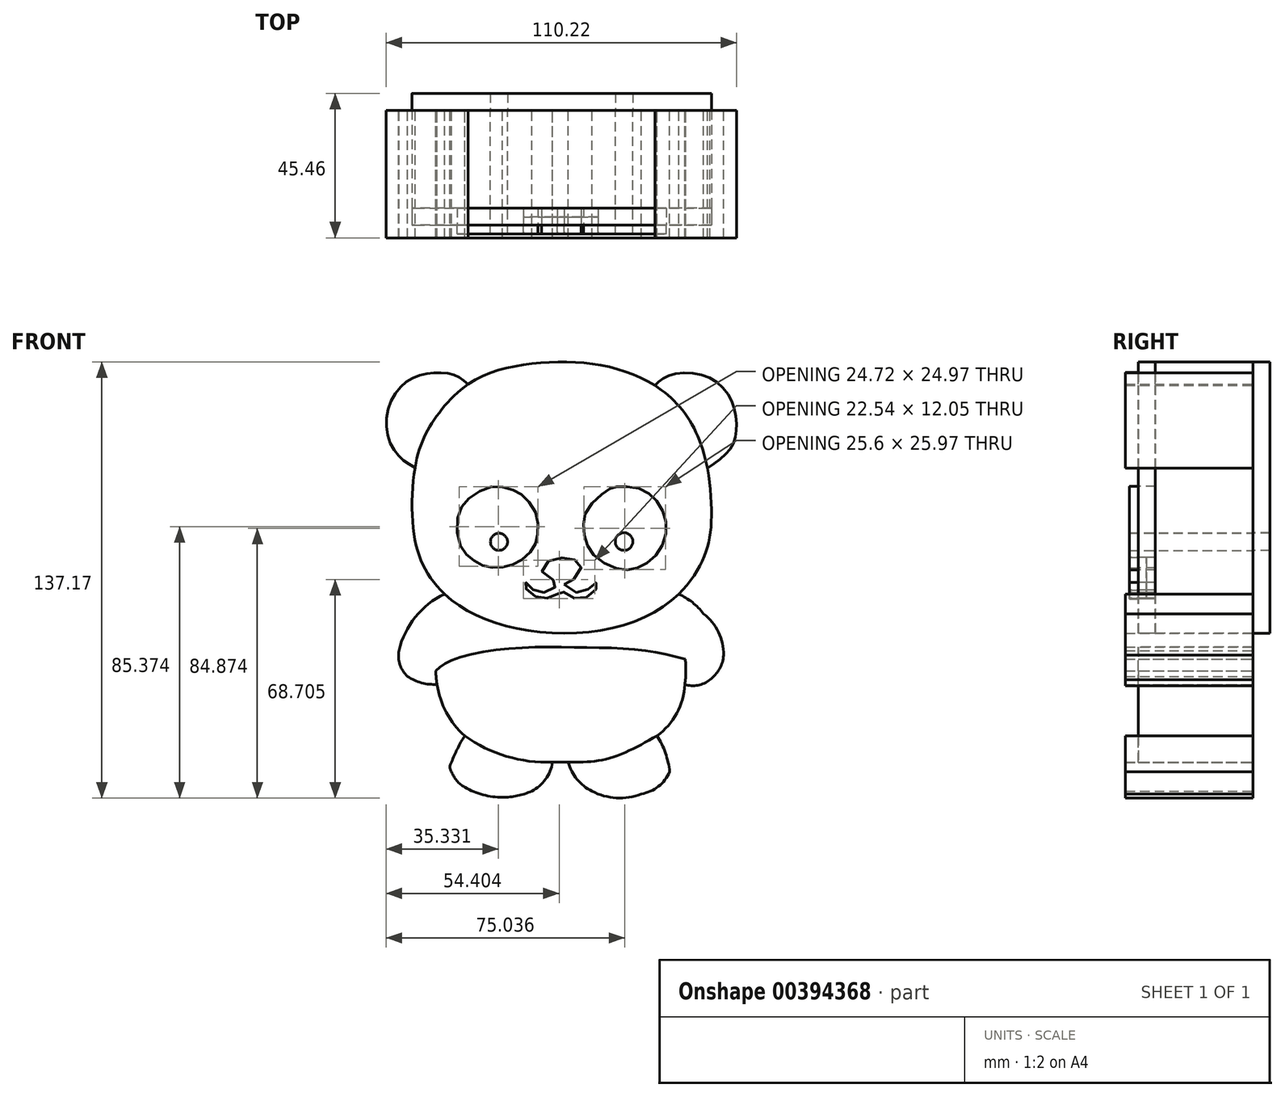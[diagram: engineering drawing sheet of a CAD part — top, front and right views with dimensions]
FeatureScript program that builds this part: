
annotation { "Feature Type Name" : "Feature", "Feature Type Description" : "" }
export const myFeature = defineFeature(function(context is Context, id is Id, definition is map)
    precondition{}
    {
        {
            var Q0;
            Q0=qCreatedBy(makeId("Front.planeOp"),FACE);
            var sketch = newSketch(context, id + "F0", { "sketchPlane" : qUnion([Q0])});
            skFitSpline(sketch, "E0", {"points": [v(-35.08, 45.27) * mm, v(-23.68, 56.67) * mm, v(-7.72, 61.99) * mm, v(10.34, 62.75) * mm, v(26.87, 59.14) * mm, v(40.17, 50.59) * mm, v(49.1, 35.2) * mm, v(51.76, 13.72) * mm, v(49.48, 1.75) * mm, v(40.74, -10.8) * mm, v(21.17, -20.67) * mm, v(-6.39, -21.43) * mm, v(-26.53, -14.4) * mm, v(-37.36, -3.76) * mm, v(-41.92, 9.92) * mm, v(-40.97, 32.15) * mm, v(-35.08, 45.27) * mm]});
            skFitSpline(sketch, "E1", {"points": [v(-41.46, 29.63) * mm, v(-47.62, 34.62) * mm, v(-50.47, 45.27) * mm, v(-45.15, 55.9) * mm, v(-36.98, 59.33) * mm, v(-29.38, 58.95) * mm, v(-24.74, 55.97) * mm], "startDerivative": vector(-42.28, 25.45) * mm, "endDerivative": vector(31.77, -26.58) * mm});
            skFitSpline(sketch, "E2", {"points": [v(34, 55.54) * mm, v(38.25, 58.65) * mm, v(49.6, 58.65) * mm, v(57.74, 51.45) * mm, v(59.66, 42.19) * mm, v(57.58, 35.48) * mm, v(50.48, 29.52) * mm], "startDerivative": vector(26.51, 27.39) * mm, "endDerivative": vector(-48.08, -32.52) * mm});
            skFitSpline(sketch, "E3", {"points": [v(21.95, 23.65) * mm, v(29.3, 23.01) * mm, v(34.9, 18.7) * mm, v(37.6, 11.35) * mm, v(35.21, 3.36) * mm, v(29.14, -1.6) * mm, v(22.9, -2.24) * mm, v(14.44, 2.56) * mm, v(11.72, 9.1) * mm, v(12.52, 16.14) * mm, v(18.91, 22.53) * mm, v(21.95, 23.65) * mm]});
            skFitSpline(sketch, "E4", {"points": [v(-17.36, 23.65) * mm, v(-11.4, 22.95) * mm, v(-7.17, 20.53) * mm, v(-3.28, 14.96) * mm, v(-2.94, 8.57) * mm, v(-4.38, 4.24) * mm, v(-9.01, 0) * mm, v(-13.77, -1.6) * mm, v(-19.12, -1.44) * mm, v(-23.36, 0.77) * mm, v(-27.05, 4.77) * mm, v(-28, 14.18) * mm, v(-24.66, 19.92) * mm, v(-17.36, 23.65) * mm]});
            skCircle(sketch, "E5", {"center": v(-15.05, 6.36) * mm, "radius": 2.68 * mm});
            skCircle(sketch, "E6", {"center": v(24.29, 6.46) * mm, "radius": 2.77 * mm});
            skFitSpline(sketch, "E7", {"points": [v(5.4, -7.03) * mm, v(9.84, -9.72) * mm, v(12.93, -8.5) * mm, v(15.08, -6.5) * mm, v(16.02, -6.9) * mm, v(15.48, -8.5) * mm, v(12.66, -11.06) * mm, v(9.16, -11.46) * mm, v(5.67, -9.85) * mm, v(4.6, -8.78) * mm, v(3.25, -10.26) * mm, v(0, -11.33) * mm, v(-3.33, -10.93) * mm, v(-6.02, -9.05) * mm, v(-7.36, -6.63) * mm, v(-6.02, -6.63) * mm, v(-4.4, -8.64) * mm, v(-1.45, -9.58) * mm, v(1.77, -8.5) * mm, v(3.25, -6.63) * mm, v(0, -4.61) * mm, v(-1.58, -1.52) * mm, v(2.98, 1.3) * mm, v(6.34, 1.17) * mm, v(10.24, 0) * mm, v(10.64, -2.46) * mm, v(7.42, -6.09) * mm, v(5.4, -7.03) * mm]});
            skArc(sketch, "E8", {"start": v(-32.16, -10.06) * mm, "mid": v(-41.36, -17.31) * mm, "end": v(-46.5, -27.85) * mm});
            skArc(sketch, "E9", {"start": v(-46.5, -27.85) * mm, "mid": v(-46.2, -32.27) * mm, "end": v(-43.8, -35.99) * mm});
            skArc(sketch, "E10", {"start": v(-43.8, -35.99) * mm, "mid": v(-39.37, -37.98) * mm, "end": v(-34.54, -38.47) * mm});
            skArc(sketch, "E11", {"start": v(-30.35, -17.77) * mm, "mid": v(-34.36, -27.73) * mm, "end": v(-34.54, -38.47) * mm});
            skArc(sketch, "E12", {"start": v(-34.54, -38.47) * mm, "mid": v(-31.6, -47.33) * mm, "end": v(-25.83, -54.65) * mm});
            skArc(sketch, "E13", {"start": v(-25.83, -54.65) * mm, "mid": v(-12.7, -61.09) * mm, "end": v(1.81, -62.96) * mm});
            skArc(sketch, "E14", {"start": v(-4.76, -72.06) * mm, "mid": v(-0.4, -68.28) * mm, "end": v(1.81, -62.96) * mm});
            skArc(sketch, "E15", {"start": v(-13.91, -73.98) * mm, "mid": v(-9.24, -73.5) * mm, "end": v(-4.76, -72.06) * mm});
            skArc(sketch, "E16", {"start": v(-25.83, -70.81) * mm, "mid": v(-20.08, -73.2) * mm, "end": v(-13.91, -73.98) * mm});
            skArc(sketch, "E17", {"start": v(-29.96, -65.96) * mm, "mid": v(-28.32, -68.74) * mm, "end": v(-25.83, -70.81) * mm});
            skArc(sketch, "E18", {"start": v(-29.96, -62.96) * mm, "mid": v(-30.47, -64.46) * mm, "end": v(-29.96, -65.96) * mm});
            skArc(sketch, "E19", {"start": v(-25.83, -54.65) * mm, "mid": v(-28.14, -58.68) * mm, "end": v(-29.96, -62.96) * mm});
            skArc(sketch, "E20", {"start": v(38.63, -65.96) * mm, "mid": v(37.31, -60.07) * mm, "end": v(34.67, -54.65) * mm});
            skArc(sketch, "E21", {"start": v(29.7, -72.96) * mm, "mid": v(35.05, -70.6) * mm, "end": v(38.63, -65.96) * mm});
            skArc(sketch, "E22", {"start": v(6.76, -62.96) * mm, "mid": v(9.5, -68.32) * mm, "end": v(14.22, -72.06) * mm});
            skArc(sketch, "E23", {"start": v(14.22, -72.06) * mm, "mid": v(21.86, -74.18) * mm, "end": v(29.7, -72.96) * mm});
            skArc(sketch, "E24", {"start": v(34.67, -54.65) * mm, "mid": v(40.87, -47.56) * mm, "end": v(43.38, -38.47) * mm});
            skArc(sketch, "E25", {"start": v(43.38, -38.47) * mm, "mid": v(43.02, -27.8) * mm, "end": v(38.63, -18.07) * mm});
            skArc(sketch, "E26", {"start": v(43.38, -38.47) * mm, "mid": v(47.55, -38.77) * mm, "end": v(51.31, -36.95) * mm});
            skArc(sketch, "E27", {"start": v(51.31, -36.95) * mm, "mid": v(54.32, -33.6) * mm, "end": v(55.61, -29.3) * mm});
            skArc(sketch, "E28", {"start": v(55.61, -29.3) * mm, "mid": v(53.98, -22.04) * mm, "end": v(49.3, -16.26) * mm});
            skArc(sketch, "E29", {"start": v(49.3, -16.26) * mm, "mid": v(45.78, -12.68) * mm, "end": v(41.49, -10.1) * mm});
            skArc(sketch, "E30", {"start": v(45.78, -9.36) * mm, "mid": v(53.67, 8.21) * mm, "end": v(53.98, 27.47) * mm});
            skPoint(sketch, "E30.startSnap0", {"position": v(45.78, -12.68) * mm});
            skPoint(sketch, "E30.endSnap0", {"position": v(53.98, -22.04) * mm});
            skArc(sketch, "E31", {"start": v(58.54, -27.85) * mm, "mid": v(54.79, -16.79) * mm, "end": v(45.78, -9.36) * mm});
            skArc(sketch, "E32", {"start": v(51.31, -41.07) * mm, "mid": v(56.55, -35.35) * mm, "end": v(58.54, -27.85) * mm});
            skArc(sketch, "E33", {"start": v(45.78, -41.07) * mm, "mid": v(48.55, -41.66) * mm, "end": v(51.31, -41.07) * mm});
            skArc(sketch, "E34", {"start": v(38.63, -54.65) * mm, "mid": v(43.06, -48.31) * mm, "end": v(45.78, -41.07) * mm});
            skArc(sketch, "E35", {"start": v(40.74, -68.63) * mm, "mid": v(40.88, -61.46) * mm, "end": v(38.63, -54.65) * mm});
            skArc(sketch, "E36", {"start": v(29.38, -76) * mm, "mid": v(35.79, -73.44) * mm, "end": v(40.74, -68.63) * mm});
            skArc(sketch, "E37", {"start": v(4.3, -65.96) * mm, "mid": v(8.42, -71.56) * mm, "end": v(14.22, -75.4) * mm});
            skArc(sketch, "E38", {"start": v(14.22, -75.4) * mm, "mid": v(21.75, -76.81) * mm, "end": v(29.38, -76) * mm});
            skArc(sketch, "E39", {"start": v(-4.76, -75.4) * mm, "mid": v(0.6, -71.48) * mm, "end": v(4.3, -65.96) * mm});
            skArc(sketch, "E40", {"start": v(-21.84, -76) * mm, "mid": v(-13.26, -76.9) * mm, "end": v(-4.76, -75.4) * mm});
            skArc(sketch, "E41", {"start": v(-32.12, -67.4) * mm, "mid": v(-27.89, -72.79) * mm, "end": v(-21.84, -76) * mm});
            skArc(sketch, "E42", {"start": v(-32.12, -62.96) * mm, "mid": v(-32.46, -65.18) * mm, "end": v(-32.12, -67.4) * mm});
            skArc(sketch, "E43", {"start": v(-29.96, -55.54) * mm, "mid": v(-31.2, -59) * mm, "end": v(-32.12, -62.54) * mm});
            skArc(sketch, "E44", {"start": v(-36.87, -41.87) * mm, "mid": v(-34.16, -49.08) * mm, "end": v(-29.96, -55.54) * mm});
            skArc(sketch, "E45", {"start": v(-49.5, -29.3) * mm, "mid": v(-45.59, -38) * mm, "end": v(-36.87, -41.87) * mm});
            skArc(sketch, "E46", {"start": v(-36.87, -9.36) * mm, "mid": v(-45.7, -17.73) * mm, "end": v(-49.5, -29.3) * mm});
            skArc(sketch, "E47", {"start": v(-43.8, 27.87) * mm, "mid": v(-44.76, 8.43) * mm, "end": v(-36.87, -9.36) * mm});
            skArc(sketch, "E48", {"start": v(-52.67, 39.14) * mm, "mid": v(-49.63, 32.4) * mm, "end": v(-43.8, 27.87) * mm});
            skArc(sketch, "E49", {"start": v(-50.3, 54.06) * mm, "mid": v(-52.52, 46.77) * mm, "end": v(-52.67, 39.14) * mm});
            skArc(sketch, "E50", {"start": v(-24.15, 59.33) * mm, "mid": v(-38.22, 61.64) * mm, "end": v(-50.3, 54.06) * mm});
            skArc(sketch, "E51", {"start": v(32.69, 59.14) * mm, "mid": v(4.3, 65.86) * mm, "end": v(-24.15, 59.33) * mm});
            skArc(sketch, "E52", {"start": v(53.98, 27.47) * mm, "mid": v(59.26, 54.01) * mm, "end": v(32.69, 59.14) * mm});
            skFitSpline(sketch, "E53", {"points": [v(-34.93, -34.2) * mm, v(-30.62, -31.16) * mm, v(-13.37, -27.32) * mm, v(9.96, -26.84) * mm, v(29.46, -27.64) * mm, v(43.51, -30.5) * mm], "startDerivative": vector(28.9, 26.69) * mm, "endDerivative": vector(69.5, -17.43) * mm});
            skFitSpline(sketch, "E54", {"points": [v(6.76, -62.96) * mm, v(19.43, -61.78) * mm, v(34.67, -54.65) * mm], "startDerivative": vector(26.94, 0.04) * mm, "endDerivative": vector(28.83, 16.2) * mm});
            skFitSpline(sketch, "E55", {"points": [v(1.81, -62.96) * mm, v(6.76, -62.96) * mm], "startDerivative": vector(4.95, 0) * mm, "endDerivative": vector(4.95, 0) * mm});
            skSolve(sketch);
        }
        {
            var Q0;
            Q0=makeQuery(id+"F0.imprint","IMPRINT",FACE,{"disambiguationData":[TD([[makeQuery(id+"F0.imprint","IMPRINT",EDGE,{"derivedFrom":sQuery(id+"F0.wireOp",EDGE,"E3")}),1.0]])]});
            var Q1;
            {var subQ1=sQuery(id+"F0.wireOp",EDGE,"E12");Q1=makeQuery(id+"F0.imprint","IMPRINT",FACE,{"disambiguationData":[TD([[makeQuery(id+"F0.imprint","IMPRINT",EDGE,{"derivedFrom":subQ1}),1.0]])]});}
            extrude(context, id + "F1", {"entities" : qUnion([Q0, Q1]), "depth" : 36.07 * mm});
        }
        {
            var Q0;
            {var subQ0=sQuery(id+"F0.wireOp",EDGE,"E1");Q0=makeQuery(id+"F0.imprint","IMPRINT",FACE,{"disambiguationData":[TD([[makeQuery(id+"F0.imprint","IMPRINT",EDGE,{"derivedFrom":subQ0}),-1.0]])]});}
            var Q1;
            {var subQ0=sQuery(id+"F0.wireOp",EDGE,"E2");Q1=makeQuery(id+"F0.imprint","IMPRINT",FACE,{"disambiguationData":[TD([[makeQuery(id+"F0.imprint","IMPRINT",EDGE,{"derivedFrom":subQ0}),-1.0]])]});}
            var Q2;
            {var subQ6=sQuery(id+"F0.wireOp",EDGE,"E8");Q2=makeQuery(id+"F0.imprint","IMPRINT",FACE,{"disambiguationData":[TD([[makeQuery(id+"F0.imprint","IMPRINT",EDGE,{"derivedFrom":subQ6}),1.0]])]});}
            var Q3;
            Q3=makeQuery(id+"F0.imprint","IMPRINT",FACE,{"disambiguationData":[TD([[makeQuery(id+"F0.imprint","IMPRINT",EDGE,{"derivedFrom":sQuery(id+"F0.wireOp",EDGE,"E20")}),1.0]])]});
            var Q4;
            Q4=makeQuery(id+"F0.imprint","IMPRINT",FACE,{"disambiguationData":[TD([[makeQuery(id+"F0.imprint","IMPRINT",EDGE,{"derivedFrom":sQuery(id+"F0.wireOp",EDGE,"E13")}),-1.0]])]});
            extrude(context, id + "F2", {"entities" : qUnion([Q0, Q1, Q2, Q3, Q4]), "depth" : 40.13 * mm});
        }
        {
            var Q0;
            Q0=makeQuery(id+"F0.imprint","IMPRINT",FACE,{"disambiguationData":[TD([[makeQuery(id+"F0.imprint","IMPRINT",EDGE,{"derivedFrom":sQuery(id+"F0.wireOp",EDGE,"E4")}),-1.0]])]});
            var Q1;
            Q1=makeQuery(id+"F0.imprint","IMPRINT",FACE,{"disambiguationData":[TD([[makeQuery(id+"F0.imprint","IMPRINT",EDGE,{"derivedFrom":sQuery(id+"F0.wireOp",EDGE,"E3")}),-1.0]])]});
            var Q2;
            Q2=makeQuery(id+"F0.imprint","IMPRINT",FACE,{"disambiguationData":[TD([[makeQuery(id+"F0.imprint","IMPRINT",EDGE,{"derivedFrom":sQuery(id+"F0.wireOp",EDGE,"E7")}),-1.0]])]});
            extrude(context, id + "F3", {"entities" : qUnion([Q0, Q1, Q2]), "operationType" : NewBodyOperationType.ADD, "depth" : 38.86 * mm});
        }
        {
            var Q0;
            Q0=makeQuery(id+"F0.imprint","IMPRINT",FACE,{"disambiguationData":[TD([[makeQuery(id+"F0.imprint","IMPRINT",EDGE,{"derivedFrom":sQuery(id+"F0.wireOp",EDGE,"E5")}),1.0]])]});
            var Q1;
            Q1=makeQuery(id+"F0.imprint","IMPRINT",FACE,{"disambiguationData":[TD([[makeQuery(id+"F0.imprint","IMPRINT",EDGE,{"derivedFrom":sQuery(id+"F0.wireOp",EDGE,"E6")}),1.0]])]});
            var Q2;
            Q2=makeQuery(id+"F1.opExtrude","CAP_FACE",FACE,{"disambiguationData":[OSD([sQuery(id+"F0.wireOp",EDGE,"E0"),sQuery(id+"F0.wireOp",EDGE,"E3"),sQuery(id+"F0.wireOp",EDGE,"E4"),sQuery(id+"F0.wireOp",EDGE,"E7")])],"isStart":false});
            var Q3;
            Q3=makeQuery(id+"F3.opExtrude","CAP_FACE",FACE,{"disambiguationData":[OSD([sQuery(id+"F0.wireOp",EDGE,"E7")])],"isStart":false});
            var Q4;
            {var subQ0=sQuery(id+"F0.wireOp",EDGE,"E7");var subQ1=sQuery(id+"F0.wireOp",EDGE,"E4");var subQ2=sQuery(id+"F0.wireOp",EDGE,"E3");Q4=makeQuery(id+"F3.boolean.opBoolean","MERGE",FACE,{"derivedFrom":[makeQuery(id+"F1.opExtrude","CAP_FACE",FACE,{"disambiguationData":[OSD([sQuery(id+"F0.wireOp",EDGE,"E0"),subQ2,subQ1,subQ0])],"isStart":true}),makeQuery(id+"F3.opExtrude","CAP_FACE",FACE,{"disambiguationData":[OSD([subQ2,sQuery(id+"F0.wireOp",EDGE,"E6")])],"isStart":true}),makeQuery(id+"F3.opExtrude","CAP_FACE",FACE,{"disambiguationData":[OSD([subQ1,sQuery(id+"F0.wireOp",EDGE,"E5")])],"isStart":true}),makeQuery(id+"F3.opExtrude","CAP_FACE",FACE,{"disambiguationData":[OSD([subQ0])],"isStart":true})]});}
            extrude(context, id + "F4", {"entities" : qUnion([Q0, Q1, Q2, Q3, Q4]), "oppositeDirection" : true, "depth" : 5.33 * mm});
        }
    });
